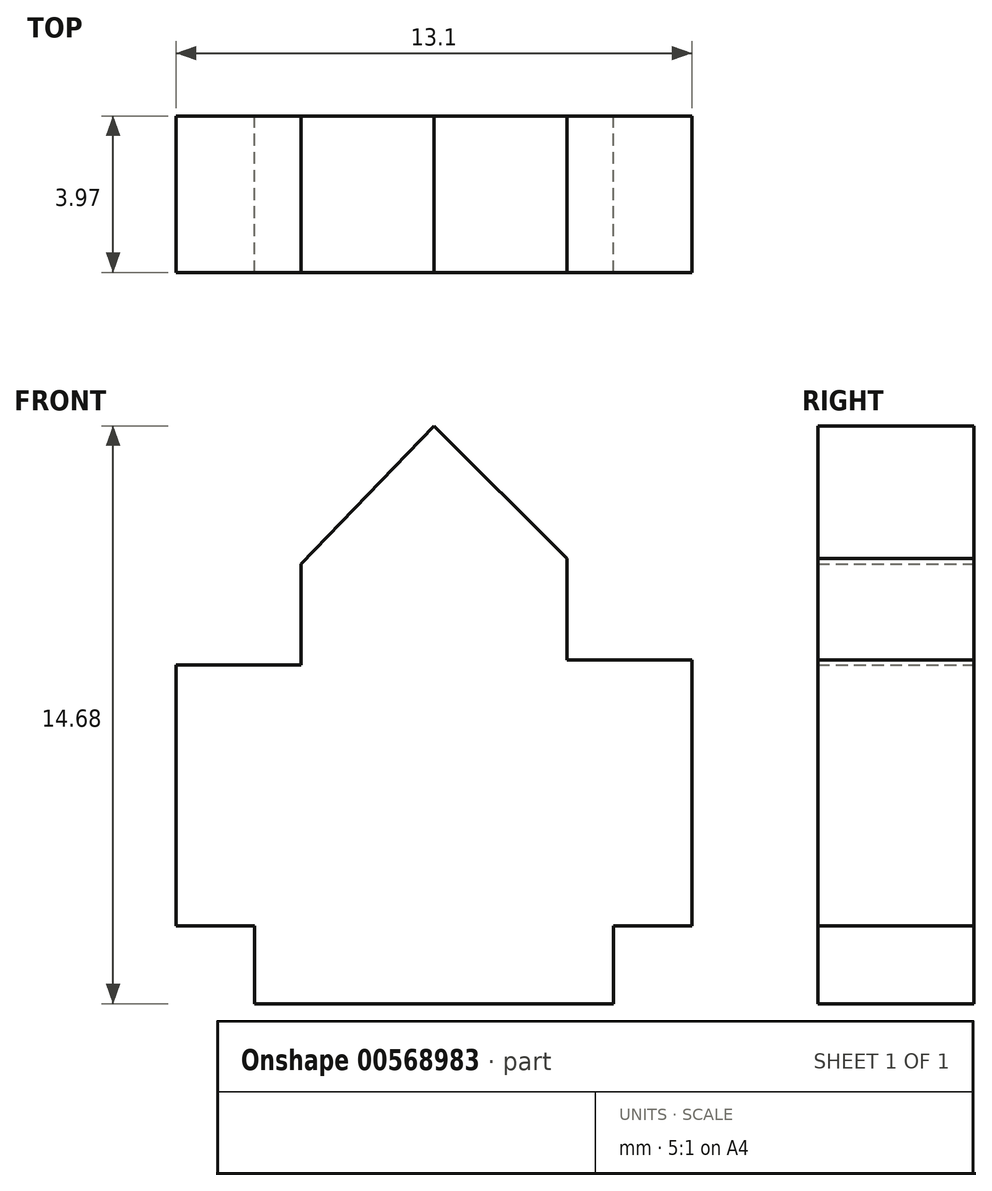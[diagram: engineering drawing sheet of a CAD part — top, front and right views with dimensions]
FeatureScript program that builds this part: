
annotation { "Feature Type Name" : "Feature", "Feature Type Description" : "" }
export const myFeature = defineFeature(function(context is Context, id is Id, definition is map)
    precondition{}
    {
        {
            var Q0;
            Q0=qCreatedBy(makeId("Front.planeOp"),FACE);
            var sketch = newSketch(context, id + "F0", { "sketchPlane" : qUnion([Q0])});
            skLineSegment(sketch, "E0", {"start": v(0, 9) * mm, "end": v(0, -5.67) * mm});
            skLineSegment(sketch, "E1", {"start": v(0, -5.67) * mm, "end": v(4.56, -5.67) * mm});
            skLineSegment(sketch, "E2", {"start": v(0, -5.67) * mm, "end": v(-4.56, -5.67) * mm});
            skLineSegment(sketch, "E3", {"start": v(-4.56, -5.67) * mm, "end": v(-4.56, -3.7) * mm});
            skLineSegment(sketch, "E4", {"start": v(4.56, -5.67) * mm, "end": v(4.56, -3.7) * mm});
            skLineSegment(sketch, "E5", {"start": v(-4.56, -3.7) * mm, "end": v(-6.55, -3.7) * mm});
            skLineSegment(sketch, "E6", {"start": v(4.56, -3.7) * mm, "end": v(6.55, -3.7) * mm});
            skLineSegment(sketch, "E7", {"start": v(-6.55, -3.7) * mm, "end": v(-6.55, 2.94) * mm});
            skLineSegment(sketch, "E8", {"start": v(6.55, -3.7) * mm, "end": v(6.55, 3.06) * mm});
            skLineSegment(sketch, "E9", {"start": v(-6.55, 2.94) * mm, "end": v(-3.37, 2.94) * mm});
            skLineSegment(sketch, "E10", {"start": v(6.55, 3.06) * mm, "end": v(3.37, 3.06) * mm});
            skLineSegment(sketch, "E11", {"start": v(-3.37, 2.94) * mm, "end": v(-3.37, 5.5) * mm});
            skLineSegment(sketch, "E12", {"start": v(3.37, 3.06) * mm, "end": v(3.37, 5.64) * mm});
            skLineSegment(sketch, "E13", {"start": v(-3.37, 5.5) * mm, "end": v(0, 9) * mm});
            skLineSegment(sketch, "E14", {"start": v(0, 9) * mm, "end": v(3.37, 5.64) * mm});
            skSolve(sketch);
        }
        {
            var Q0;
            Q0 = qSketchRegion(id + "F0", true);
            extrude(context, id + "F1", {"entities" : qUnion([Q0]), "depth" : 3.97 * mm, "offsetDistance" : 25.4 * mm});
        }
    });
